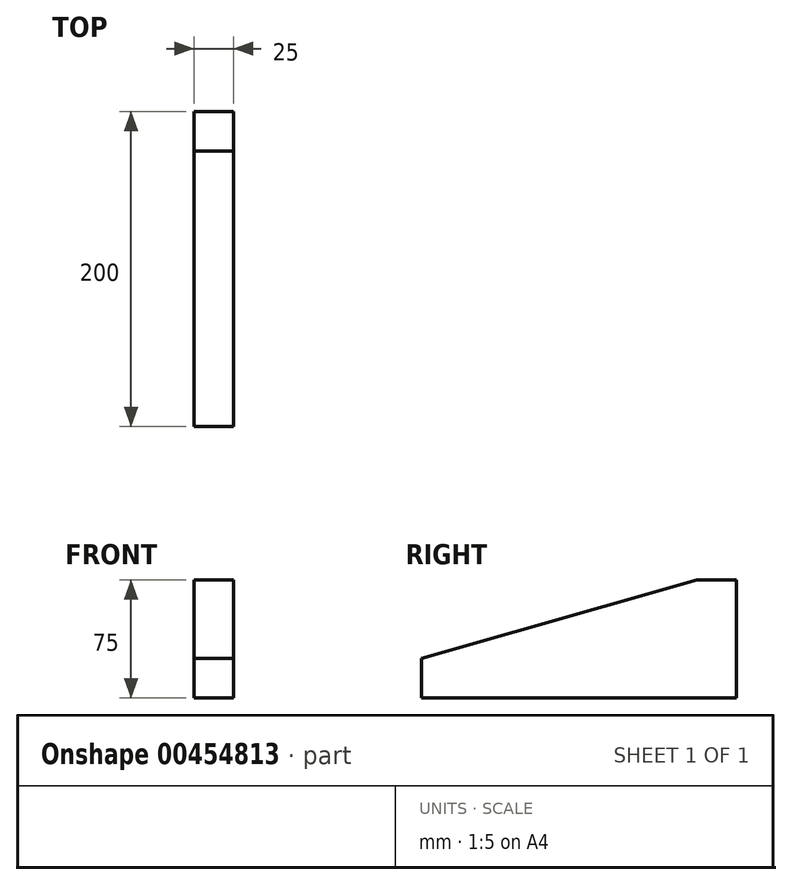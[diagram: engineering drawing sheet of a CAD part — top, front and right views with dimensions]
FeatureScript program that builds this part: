
annotation { "Feature Type Name" : "Feature", "Feature Type Description" : "" }
export const myFeature = defineFeature(function(context is Context, id is Id, definition is map)
    precondition{}
    {
        {
            var Q0;
            Q0=qCreatedBy(makeId("Right.planeOp"),FACE);
            var sketch = newSketch(context, id + "F0", { "sketchPlane" : qUnion([Q0])});
            skLineSegment(sketch, "E0.bottom", {"start": v(0, 0) * mm, "end": v(-200, 0) * mm});
            skLineSegment(sketch, "E0.top", {"start": v(0, 25) * mm, "end": v(-200, 25) * mm});
            skLineSegment(sketch, "E0.left", {"start": v(0, 0) * mm, "end": v(0, 25) * mm});
            skLineSegment(sketch, "E0.right", {"start": v(-200, 0) * mm, "end": v(-200, 25) * mm});
            skLineSegment(sketch, "E1.bottom", {"start": v(0, 25) * mm, "end": v(-25, 25) * mm});
            skLineSegment(sketch, "E1.top", {"start": v(0, 75) * mm, "end": v(-25, 75) * mm});
            skLineSegment(sketch, "E1.left", {"start": v(0, 25) * mm, "end": v(0, 75) * mm});
            skLineSegment(sketch, "E1.right", {"start": v(-25, 25) * mm, "end": v(-25, 75) * mm});
            skLineSegment(sketch, "E2", {"start": v(-25, 75) * mm, "end": v(-200, 25) * mm});
            skSolve(sketch);
        }
        {
            var Q0;
            Q0 = qSketchRegion(id + "F0", true);
            extrude(context, id + "F1", {"entities" : qUnion([Q0]), "depth" : 25 * mm});
        }
    });
